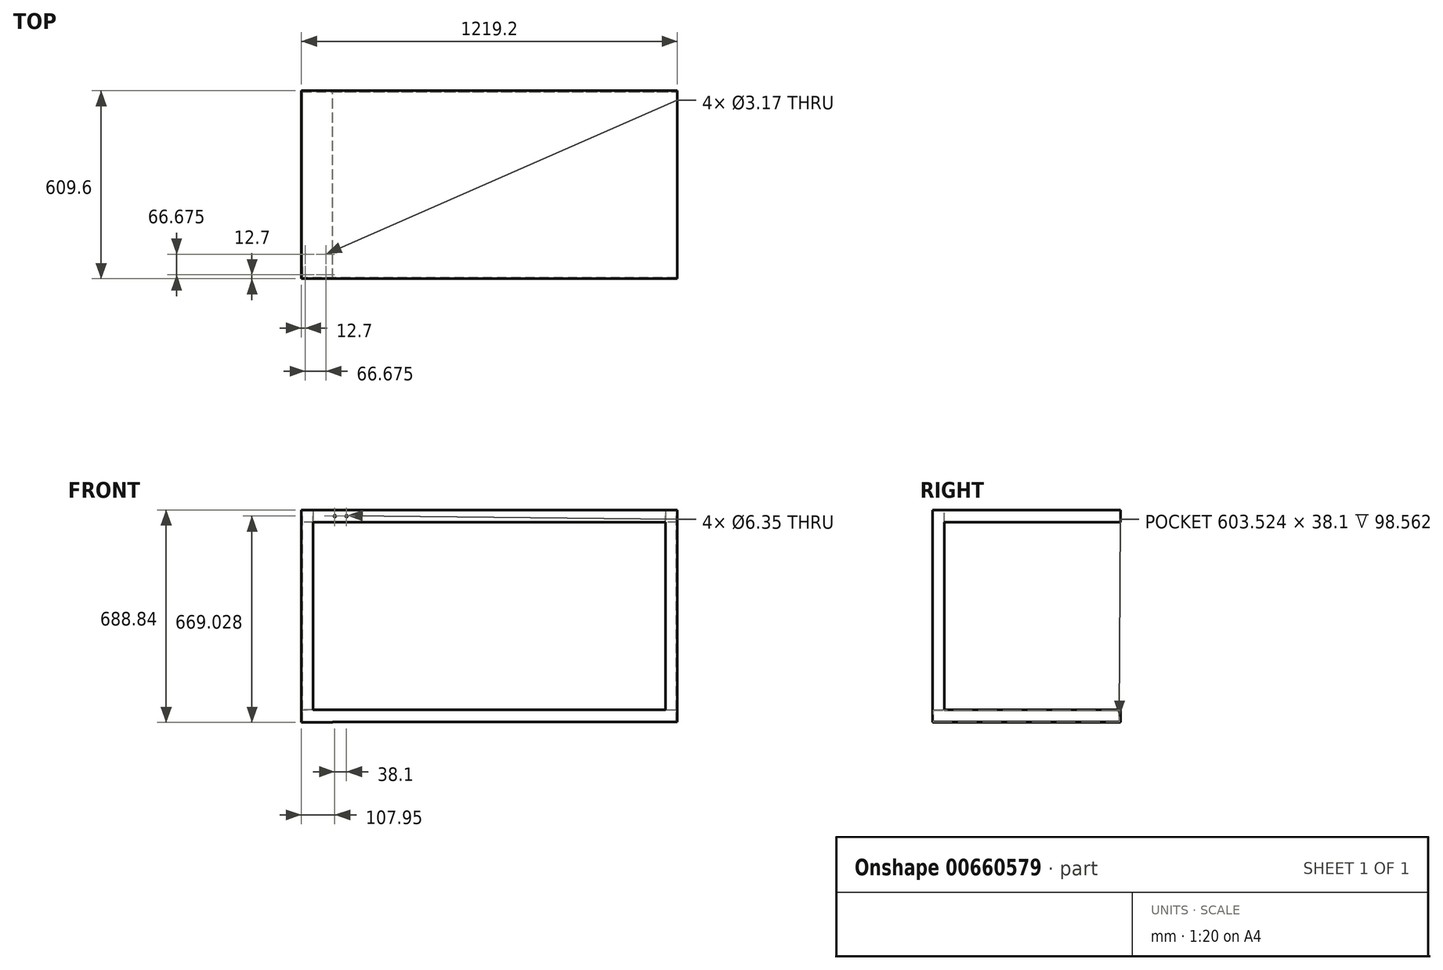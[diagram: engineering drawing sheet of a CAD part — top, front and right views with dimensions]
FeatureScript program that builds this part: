
annotation { "Feature Type Name" : "Feature", "Feature Type Description" : "" }
export const myFeature = defineFeature(function(context is Context, id is Id, definition is map)
    precondition{}
    {
        {
            var Q0;
            Q0=qCreatedBy(makeId("Top.planeOp"),FACE);
            var sketch = newSketch(context, id + "F0", { "sketchPlane" : qUnion([Q0])});
            skLineSegment(sketch, "E0.bottom", {"start": v(609.6, 304.8) * mm, "end": v(-609.6, 304.8) * mm});
            skLineSegment(sketch, "E0.top", {"start": v(609.6, -304.8) * mm, "end": v(-609.6, -304.8) * mm});
            skLineSegment(sketch, "E0.left", {"start": v(609.6, 304.8) * mm, "end": v(609.6, -304.8) * mm});
            skLineSegment(sketch, "E0.right", {"start": v(-609.6, 304.8) * mm, "end": v(-609.6, -304.8) * mm});
            skPoint(sketch, "E0.middle", {"position": v(0, 0) * mm});
            skSolve(sketch);
        }
        {
            var Q0;
            Q0 = qSketchRegion(id + "F0", true);
            extrude(context, id + "F1", {"entities" : qUnion([Q0]), "oppositeDirection" : true, "depth" : 1.52 * mm, "offsetDistance" : 25.4 * mm});
        }
        {
            var Q0;
            Q0=makeQuery(id+"F1.opExtrude","CAP_FACE",FACE,{"disambiguationData":[OSD([sQuery(id+"F0.wireOp",EDGE,"E0.bottom"),sQuery(id+"F0.wireOp",EDGE,"E0.top"),sQuery(id+"F0.wireOp",EDGE,"E0.left"),sQuery(id+"F0.wireOp",EDGE,"E0.right")])],"isStart":false});
            var sketch = newSketch(context, id + "F2", { "sketchPlane" : qUnion([Q0])});
            skLineSegment(sketch, "E1", {"start": v(-609.6, 304.8) * mm, "end": v(609.6, 304.8) * mm});
            skLineSegment(sketch, "E2", {"start": v(609.6, 304.8) * mm, "end": v(609.6, -304.8) * mm});
            skLineSegment(sketch, "E3", {"start": v(609.6, -304.8) * mm, "end": v(-609.6, -304.8) * mm});
            skLineSegment(sketch, "E4", {"start": v(-609.6, -304.8) * mm, "end": v(-609.6, 304.8) * mm});
            skLineSegment(sketch, "E5.0", {"start": v(-608.08, -303.28) * mm, "end": v(-608.08, 303.28) * mm});
            skLineSegment(sketch, "E6.0", {"start": v(-608.08, 303.28) * mm, "end": v(608.08, 303.28) * mm});
            skLineSegment(sketch, "E7.0", {"start": v(608.08, 303.28) * mm, "end": v(608.08, -303.28) * mm});
            skLineSegment(sketch, "E8.0", {"start": v(608.08, -303.28) * mm, "end": v(-608.08, -303.28) * mm});
            skSolve(sketch);
        }
        {
            var Q0;
            Q0 = qSketchRegion(id + "F2", true);
            extrude(context, id + "F3", {"entities" : qUnion([Q0]), "operationType" : NewBodyOperationType.ADD, "depth" : 38.1 * mm, "offsetDistance" : 25.4 * mm});
        }
        {
            var Q0;
            Q0=makeQuery(id+"F1.opExtrude","CAP_FACE",FACE,{"disambiguationData":[OSD([sQuery(id+"F0.wireOp",EDGE,"E0.bottom"),sQuery(id+"F0.wireOp",EDGE,"E0.top"),sQuery(id+"F0.wireOp",EDGE,"E0.left"),sQuery(id+"F0.wireOp",EDGE,"E0.right")])],"isStart":false});
            var sketch = newSketch(context, id + "F4", { "sketchPlane" : qUnion([Q0])});
            skLineSegment(sketch, "E9", {"start": v(-571.5, 304.8) * mm, "end": v(-609.6, 304.8) * mm});
            skLineSegment(sketch, "E10", {"start": v(-609.6, 304.8) * mm, "end": v(-609.6, 266.7) * mm});
            skLineSegment(sketch, "E11", {"start": v(-609.6, 266.7) * mm, "end": v(-606.56, 266.7) * mm});
            skLineSegment(sketch, "E12", {"start": v(-606.56, 266.7) * mm, "end": v(-606.56, 301.76) * mm});
            skLineSegment(sketch, "E13", {"start": v(-606.56, 301.76) * mm, "end": v(-571.5, 301.76) * mm});
            skLineSegment(sketch, "E14", {"start": v(-571.5, 301.76) * mm, "end": v(-571.5, 304.8) * mm});
            skLineSegment(sketch, "E15.MirrorCS", {"start": v(571.5, 301.76) * mm, "end": v(571.5, 304.8) * mm});
            skLineSegment(sketch, "E16.MirrorCS", {"start": v(609.6, 266.7) * mm, "end": v(606.56, 266.7) * mm});
            skLineSegment(sketch, "E17.MirrorCS", {"start": v(606.56, 301.76) * mm, "end": v(571.5, 301.76) * mm});
            skLineSegment(sketch, "E18.MirrorCS", {"start": v(606.56, 266.7) * mm, "end": v(606.56, 301.76) * mm});
            skLineSegment(sketch, "E19.MirrorCS", {"start": v(571.5, 304.8) * mm, "end": v(609.6, 304.8) * mm});
            skLineSegment(sketch, "E20.MirrorCS", {"start": v(609.6, 304.8) * mm, "end": v(609.6, 266.7) * mm});
            skSolve(sketch);
        }
        {
            var Q0;
            Q0 = qSketchRegion(id + "F4", true);
            extrude(context, id + "F5", {"entities" : qUnion([Q0]), "operationType" : NewBodyOperationType.ADD, "depth" : 685.8 * mm, "offsetDistance" : 25.4 * mm});
        }
        {
            var Q0;
            Q0=makeQuery(id+"F1.opExtrude","CAP_FACE",FACE,{"disambiguationData":[OSD([sQuery(id+"F0.wireOp",EDGE,"E0.bottom"),sQuery(id+"F0.wireOp",EDGE,"E0.top"),sQuery(id+"F0.wireOp",EDGE,"E0.left"),sQuery(id+"F0.wireOp",EDGE,"E0.right")])],"isStart":true});
            cPlane(context, id + "F6", {"entities" : qUnion([Q0]), "cplaneType" : CPlaneType.OFFSET, "offset" : 647.7 * mm, "oppositeDirection" : true, "width" : 152.4 * mm, "height" : 152.4 * mm});
        }
        {
            var Q0;
            Q0=qCreatedBy(id+"F6.planeOp",FACE);
            var sketch = newSketch(context, id + "F7", { "sketchPlane" : qUnion([Q0])});
            skLineSegment(sketch, "E21.bottom", {"start": v(-609.6, 304.8) * mm, "end": v(609.6, 304.8) * mm});
            skLineSegment(sketch, "E21.top", {"start": v(-609.6, -304.8) * mm, "end": v(609.6, -304.8) * mm});
            skLineSegment(sketch, "E21.left", {"start": v(-609.6, 304.8) * mm, "end": v(-609.6, -304.8) * mm});
            skLineSegment(sketch, "E21.right", {"start": v(609.6, 304.8) * mm, "end": v(609.6, -304.8) * mm});
            skPoint(sketch, "E21.middle", {"position": v(0, 0) * mm});
            skSolve(sketch);
        }
        {
            var Q0;
            Q0 = qSketchRegion(id + "F7", true);
            extrude(context, id + "F8", {"entities" : qUnion([Q0]), "operationType" : NewBodyOperationType.ADD, "oppositeDirection" : true, "depth" : 1.52 * mm, "offsetDistance" : 25.4 * mm});
        }
        {
            var Q0;
            Q0=makeQuery(id+"F8.opExtrude","CAP_FACE",FACE,{"disambiguationData":[OSD([sQuery(id+"F7.wireOp",EDGE,"E21.bottom"),sQuery(id+"F7.wireOp",EDGE,"E21.top"),sQuery(id+"F7.wireOp",EDGE,"E21.left"),sQuery(id+"F7.wireOp",EDGE,"E21.right")])],"isStart":false});
            var sketch = newSketch(context, id + "F9", { "sketchPlane" : qUnion([Q0])});
            skLineSegment(sketch, "E22.bottom", {"start": v(-609.6, 304.8) * mm, "end": v(609.6, 304.8) * mm});
            skLineSegment(sketch, "E22.top", {"start": v(-609.6, -304.8) * mm, "end": v(609.6, -304.8) * mm});
            skLineSegment(sketch, "E22.left", {"start": v(-609.6, 304.8) * mm, "end": v(-609.6, -304.8) * mm});
            skLineSegment(sketch, "E22.right", {"start": v(609.6, 304.8) * mm, "end": v(609.6, -304.8) * mm});
            skPoint(sketch, "E22.middle", {"position": v(0, 0) * mm});
            skLineSegment(sketch, "E23.bottom", {"start": v(-606.56, 301.76) * mm, "end": v(606.56, 301.76) * mm});
            skLineSegment(sketch, "E23.top", {"start": v(-606.56, -301.76) * mm, "end": v(606.56, -301.76) * mm});
            skLineSegment(sketch, "E23.left", {"start": v(-606.56, 301.76) * mm, "end": v(-606.56, -301.76) * mm});
            skLineSegment(sketch, "E23.right", {"start": v(606.56, 301.76) * mm, "end": v(606.56, -301.76) * mm});
            skSolve(sketch);
        }
        {
            var Q0;
            Q0 = qSketchRegion(id + "F9", true);
            extrude(context, id + "F10", {"entities" : qUnion([Q0]), "operationType" : NewBodyOperationType.ADD, "depth" : 38.1 * mm, "offsetDistance" : 25.4 * mm});
        }
        {
            var Q0;
            {var subQ0=sQuery(id+"F4.wireOp",EDGE,"E19.MirrorCS");var subQ1=sQuery(id+"F4.wireOp",EDGE,"E20.MirrorCS");var subQ2=sQuery(id+"F4.wireOp",EDGE,"E17.MirrorCS");var subQ3=sQuery(id+"F4.wireOp",EDGE,"E15.MirrorCS");var subQ4=sQuery(id+"F4.wireOp",EDGE,"E16.MirrorCS");var subQ5=sQuery(id+"F4.wireOp",EDGE,"E18.MirrorCS");var subQ6=sQuery(id+"F4.wireOp",EDGE,"E9");var subQ7=sQuery(id+"F4.wireOp",EDGE,"E10");var subQ8=sQuery(id+"F4.wireOp",EDGE,"E13");var subQ9=sQuery(id+"F4.wireOp",EDGE,"E14");var subQ10=sQuery(id+"F4.wireOp",EDGE,"E12");var subQ11=sQuery(id+"F4.wireOp",EDGE,"E11");Q0=makeQuery(id+"F10.boolean.opBoolean","MERGE",FACE,{"derivedFrom":[makeQuery(id+"F5.opExtrude","CAP_FACE",FACE,{"disambiguationData":[OSD([subQ11,subQ10,subQ9,subQ8,subQ7,subQ6])],"isStart":false}),makeQuery(id+"F5.opExtrude","CAP_FACE",FACE,{"disambiguationData":[OSD([subQ5,subQ4,subQ3,subQ2,subQ1,subQ0])],"isStart":false}),makeQuery(id+"F0JGexphdKmqHas_1.1.F5.opExtrude","CAP_FACE",FACE,{"disambiguationData":[OSD([subQ11,subQ10,subQ9,subQ8,subQ7,subQ6])],"isStart":false}),makeQuery(id+"F0JGexphdKmqHas_1.1.F5.opExtrude","CAP_FACE",FACE,{"disambiguationData":[OSD([subQ5,subQ4,subQ3,subQ2,subQ1,subQ0])],"isStart":false}),makeQuery(id+"F10.opExtrude","CAP_FACE",FACE,{"disambiguationData":[OSD([sQuery(id+"F9.wireOp",EDGE,"E22.bottom"),sQuery(id+"F9.wireOp",EDGE,"E22.top"),sQuery(id+"F9.wireOp",EDGE,"E22.left"),sQuery(id+"F9.wireOp",EDGE,"E22.right"),sQuery(id+"F9.wireOp",EDGE,"E23.bottom"),sQuery(id+"F9.wireOp",EDGE,"E23.top"),sQuery(id+"F9.wireOp",EDGE,"E23.left"),sQuery(id+"F9.wireOp",EDGE,"E23.right")])],"isStart":false})]});}
            var sketch = newSketch(context, id + "F11", { "sketchPlane" : qUnion([Q0])});
            skLineSegment(sketch, "E24.bottom", {"start": v(-609.6, 304.8) * mm, "end": v(-508, 304.8) * mm});
            skLineSegment(sketch, "E24.top", {"start": v(-609.6, -304.8) * mm, "end": v(-508, -304.8) * mm});
            skLineSegment(sketch, "E24.left", {"start": v(-609.6, 304.8) * mm, "end": v(-609.6, -304.8) * mm});
            skLineSegment(sketch, "E24.right", {"start": v(-508, 304.8) * mm, "end": v(-508, -304.8) * mm});
            skSolve(sketch);
        }
        {
            var Q0;
            Q0 = qSketchRegion(id + "F11", true);
            extrude(context, id + "F12", {"entities" : qUnion([Q0]), "operationType" : NewBodyOperationType.ADD, "depth" : 1.52 * mm, "offsetDistance" : 25.4 * mm});
        }
        {
            var Q0;
            Q0=makeQuery(id+"F12.opExtrude","CAP_FACE",FACE,{"disambiguationData":[OSD([sQuery(id+"F11.wireOp",EDGE,"E24.bottom"),sQuery(id+"F11.wireOp",EDGE,"E24.top"),sQuery(id+"F11.wireOp",EDGE,"E24.left"),sQuery(id+"F11.wireOp",EDGE,"E24.right")])],"isStart":false});
            var sketch = newSketch(context, id + "F13", { "sketchPlane" : qUnion([Q0])});
            skCircle(sketch, "E25", {"center": v(-596.9, 292.1) * mm, "radius": 1.59 * mm});
            skCircle(sketch, "E26", {"center": v(-596.9, 225.43) * mm, "radius": 1.59 * mm});
            skCircle(sketch, "E27", {"center": v(-530.22, 292.1) * mm, "radius": 1.59 * mm});
            skCircle(sketch, "E28", {"center": v(-530.22, 225.43) * mm, "radius": 1.59 * mm});
            skSolve(sketch);
        }
        {
            var Q0;
            Q0 = qSketchRegion(id + "F13", true);
            extrude(context, id + "F14", {"entities" : qUnion([Q0]), "operationType" : NewBodyOperationType.REMOVE, "oppositeDirection" : true, "depth" : 1.65 * mm, "offsetDistance" : 25.4 * mm});
        }
        {
            var Q0;
            {var subQ0=sQuery(id+"F11.wireOp",EDGE,"E24.bottom");Q0=makeQuery(id+"FFECTHleiI08KKR_1.1.F12.boolean.opBoolean","MERGE",FACE,{"derivedFrom":[makeQuery(id+"F12.boolean.opBoolean","MERGE",FACE,{"derivedFrom":[makeQuery(id+"F10.boolean.opBoolean","MERGE",FACE,{"derivedFrom":[makeQuery(id+"F8.boolean.opBoolean","MERGE",FACE,{"derivedFrom":[makeQuery(id+"F5.boolean.opBoolean","MERGE",FACE,{"derivedFrom":[makeQuery(id+"F3.boolean.opBoolean","MERGE",FACE,{"derivedFrom":[makeQuery(id+"F1.opExtrude","SWEPT_FACE",FACE,{"disambiguationData":[OSD([sQuery(id+"F0.wireOp",EDGE,"E0.top")])]}),makeQuery(id+"F3.opExtrude","SWEPT_FACE",FACE,{"disambiguationData":[OSD([sQuery(id+"F2.wireOp",EDGE,"E1")])]})]}),makeQuery(id+"F5.opExtrude","SWEPT_FACE",FACE,{"disambiguationData":[OSD([sQuery(id+"F4.wireOp",EDGE,"E19.MirrorCS")])]}),makeQuery(id+"F5.opExtrude","SWEPT_FACE",FACE,{"disambiguationData":[OSD([sQuery(id+"F4.wireOp",EDGE,"E9")])]})]}),makeQuery(id+"F8.opExtrude","SWEPT_FACE",FACE,{"disambiguationData":[OSD([sQuery(id+"F7.wireOp",EDGE,"E21.top")])]})]}),makeQuery(id+"F10.opExtrude","SWEPT_FACE",FACE,{"disambiguationData":[OSD([sQuery(id+"F9.wireOp",EDGE,"E22.bottom")])]})]}),makeQuery(id+"F12.opExtrude","SWEPT_FACE",FACE,{"disambiguationData":[OSD([subQ0])]})]}),makeQuery(id+"FFECTHleiI08KKR_1.1.F12.opExtrude","SWEPT_FACE",FACE,{"disambiguationData":[OSD([subQ0])]})]});}
            var sketch = newSketch(context, id + "F15", { "sketchPlane" : qUnion([Q0])});
            skPoint(sketch, "E29", {"position": v(-463.55, -19.81) * mm});
            skPoint(sketch, "E30", {"position": v(-501.65, -19.81) * mm});
            skSolve(sketch);
        }
        {
            var Q0;
            Q0=sQuery(id+"F15.wireOp",VERTEX,"E30");
            var Q1;
            Q1=sQuery(id+"F15.wireOp",VERTEX,"E29");
            var Q2;
            Q2=makeQuery(id+"F1.opExtrude","SWEPT_BODY",BODY,{"disambiguationData":[OSD([sQuery(id+"F0.wireOp",EDGE,"E0.bottom"),sQuery(id+"F0.wireOp",EDGE,"E0.top"),sQuery(id+"F0.wireOp",EDGE,"E0.left"),sQuery(id+"F0.wireOp",EDGE,"E0.right")])]});
            hole(context, id + "F16", {"style" : HoleStyle.SIMPLE, "endStyle" : HoleEndStyle.THROUGH, "holeDiameter" : 6.35 * mm, "majorDiameter" : 6.35 * mm, "isTappedThrough" : true, "tappedDepth" : 12.7 * mm, "tapClearance" : 3, "startFromSketch" : true, "locations" : qUnion([Q0, Q1]), "scope" : qUnion([Q2])});
        }
    });
